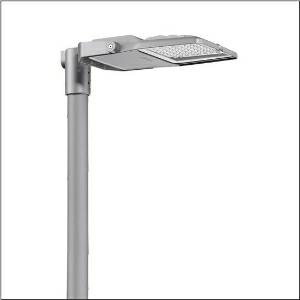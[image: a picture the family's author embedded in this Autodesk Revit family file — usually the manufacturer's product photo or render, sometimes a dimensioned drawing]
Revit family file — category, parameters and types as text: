
# Revit family: floodlight_fl_21_mini___pl33t_5xa7775d2f3a_2fb5
name_source: partatom
category: Lighting Fixtures
units: mm (PartAtom-declared; Revit-internal decimal feet)

## family parameters
Cut with Voids When Loaded = No
Host = Face
Light Source = No
Part Type = Normal
Room Calculation Point = No
Round Connector Dimension = Use Diameter
Shared = No

## types (1)
- --- (1 x LED, 17630 lm, 142.9 W, 3000K)
    Apparent Load = 143 VA
    CIE Flux Codes = 26 75 99 100 100
    Color Rendering = 70
    Color Temperature = 3000K
    Default Elevation = 1800 mm
    Description = Floodlight FL 21 mini, floodlight, primary light control with lens, of PMMA, primary optical cover: protective disc, of toughened safety glass, transparent, light distribution: PL33T, light emission: direct distribution, installation type: surface-mounted, LED, High Power LED, rated luminous flux: 17.630lm, luminous efficacy: 123lm/W, light colour: 730, colour temperature: 3000K, control gear: Smart Interface (Zhaga), control: flexible luminous flux parameterisation, time-dependent luminous flux control, constant luminous flux control, overheat protection, pre-setting: logarithmic dimming characteristic, with terminal, 6-pole, mains connection: 220..240V, AC, 50/60Hz, start of lifetime: 143W, end of service life: 151W, reduction: 63W, luminaire housing, of diecast aluminium, powder-coated, Siteco® metallic grey (DB 702S), corrosivity category C5 mid according to DIN EN ISO 12944, suitable for swimming pools, chlorine-resistant, sealing non-destructively replaceable, please order mast flange separately, mast bracket, of steel, galvanised, powder-coated, Siteco® metallic grey (DB 702S), Smart Interface above, protection rating (complete): IP66, insulation class (complete): insulation class II (safety insulation), certification: CE, ENEC, VDE, protection symbol: D, impact resistance: IK08, permissible operating ambient temperature: -40..+40°C, permissible operating ambient temperature for outdoor applications: -40..+50°C, standard: DIN EN 12944, LABS conformity tested according to VDMA 24364:2018-05, packaging unit: 1 piece

Light Distribution: PL33T
    Height = 70 mm
    Lamp = 1 x LED
    Lamp Light Flux = 17630 lm
    Lamp Power = 142.9 W
    Lamp count = 1
    Length = 485 mm
    Luminous efficacy = 123 lm/W
    Manufacturer = Siteco
    ModVariant = No
    Model = 5XA7775D2F3A
    Number of Poles = 1
    OnlyDefault = Yes
    Power Factor = 1
    Product Name = Floodlight FL 21 mini | PL33T
    Product group = floodlight | pylon annexe
    ProductGroupID = 6201
    Protection Class = Protection class II
    Protection Degree = IP 66
    RLX_Detail_Level = 1
    RLX_Emergency_Light_Flux = 0 lm
    RLX_Emergency_Type = 0
    RLX_Emergency_Type_DB = No
    RlxData = <blob elided: 101321 chars, md5=e4af1755>
    Socket = socket
    Standby Power = 0 W
    System Light Flux = 17630 lm
    System Power = 143 W
    Type Comments = factory setting: luminous flux: 100 % | dim-lin: 254 | 730 mA
    Type Image = l_1007125.jpg
    URL = http://relux.com
    VarID = @adj_169839
    Voltage = 0 V
    Weight = 0.00 kg
    Width = 337 mm

## geometry (parser evidence)
native form markers: Blend x4, Sweep x11
no freeform markers — native parametric forms only
